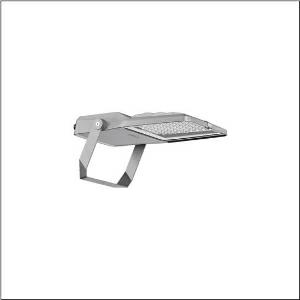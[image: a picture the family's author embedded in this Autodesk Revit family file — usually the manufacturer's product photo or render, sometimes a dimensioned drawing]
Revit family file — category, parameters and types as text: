
# Revit family: floodlight_fl_21_iq_mini___rs12_5xa7772c4b1a_5071
name_source: partatom
category: Lighting Fixtures
units: mm (PartAtom-declared; Revit-internal decimal feet)

## family parameters
Cut with Voids When Loaded = No
Host = Face
Light Source = No
Part Type = Normal
Room Calculation Point = No
Round Connector Dimension = Use Diameter
Shared = No

## types (1)
- --- (1 x LED, 12860 lm, 87.2 W, 4000K)
    Apparent Load = 87 VA
    CIE Flux Codes = 79 92 99 100 100
    Color Rendering = 70
    Color Temperature = 4000K
    Default Elevation = 1800 mm
    Description = Floodlight FL 21 iQ mini, floodlight, primary light control with lens, of PMMA, primary optical cover: protective disc, of toughened safety glass, transparent, light distribution: RS12, light emission: direct distribution, installation type: surface-mounted, LED, High Power LED, rated luminous flux: 12.860lm, luminous efficacy: 148lm/W, light colour: 740, colour temperature: 4000K, control gear: iQ Street-Remote/DALI, control: Street-Remote, Auto-Match, Temp-Guard, Night-Set, Smart-Wire, Desk-Remote (wireless, voltage-free reading and setting of iQ features in the workshop via application-optimized NFC function/RFID function), optimised constant luminous flux control (CLO 2.0), with terminal, 6-pole, mains connection: 220..240V, AC, 50/60Hz, start of lifetime: 87W, end of service life: 92W, reduction: 40W, luminaire housing, of diecast aluminium, powder-coated, Siteco® metallic grey (DB 702S), corrosivity category C5 mid according to DIN EN ISO 12944, suitable for swimming pools, chlorine-resistant, sealing non-destructively replaceable, mounting bracket, of steel, galvanised, powder-coated, Siteco® metallic grey (DB 702S), protection rating (complete): IP66, insulation class (complete): insulation class II (safety insulation), certification: CE, ENEC, VDE, protection symbol: D, impact resistance: IK08, permissible operating ambient temperature: -40..+40°C, permissible operating ambient temperature for outdoor applications: -40..+50°C, standard: DIN EN 12944, LABS conformity tested according to VDMA 24364:2018-05, packaging unit: 1 piece

Light Distribution: RS12
    Height = 70 mm
    Lamp = 1 x LED
    Lamp Light Flux = 12860 lm
    Lamp Power = 87.2 W
    Lamp count = 1
    Length = 485 mm
    Luminous efficacy = 147 lm/W
    Manufacturer = Siteco
    ModVariant = No
    Model = 5XA7772C4B1A
    Number of Poles = 1
    OnlyDefault = Yes
    Power Factor = 1
    Product Name = Floodlight FL 21 iQ mini | RS12
    Product group = floodlight | pylon annexe
    ProductGroupID = 6200
    Protection Class = Protection class II
    Protection Degree = IP 66
    RLX_Detail_Level = 1
    RLX_Emergency_Light_Flux = 0 lm
    RLX_Emergency_Type = 0
    RLX_Emergency_Type_DB = No
    RlxData = <blob elided: 91149 chars, md5=2214c173>
    Socket = socket
    Standby Power = 0 W
    System Light Flux = 12860 lm
    System Power = 87 W
    Type Comments = factory setting: luminous flux: 100 % | dim-lin: 254 | 456 mA
    Type Image = l_1006845.jpg
    URL = http://relux.com
    VarID = @adj_167564
    Voltage = 0 V
    Weight = 0.00 kg
    Width = 337 mm

## geometry (parser evidence)
native form markers: Blend x4, Sweep x13
no freeform markers — native parametric forms only
